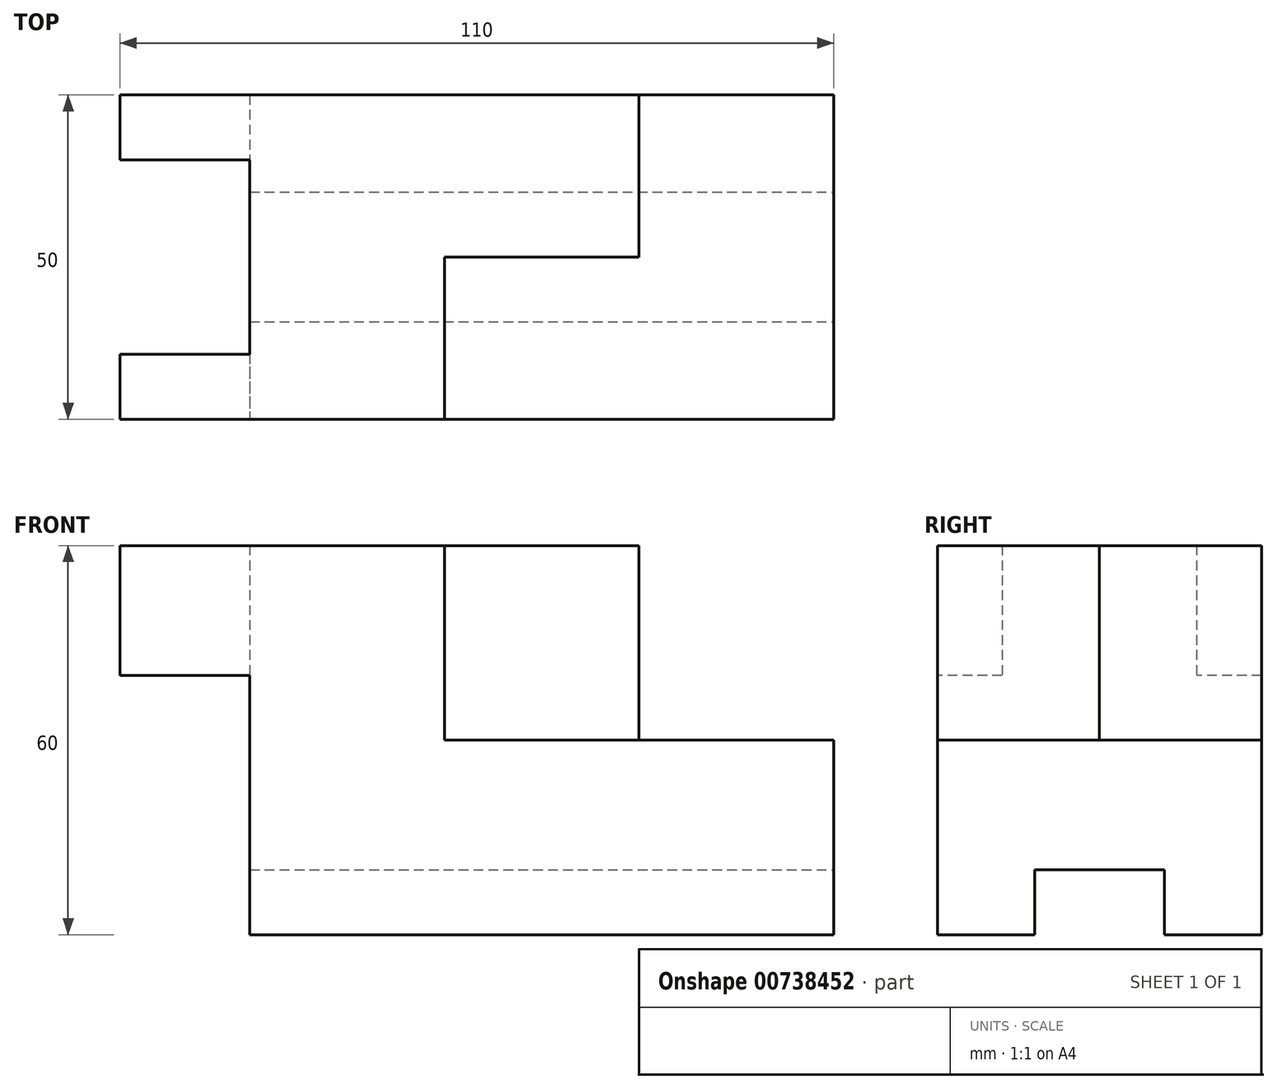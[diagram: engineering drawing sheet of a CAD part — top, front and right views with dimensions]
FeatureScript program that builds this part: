
annotation { "Feature Type Name" : "Feature", "Feature Type Description" : "" }
export const myFeature = defineFeature(function(context is Context, id is Id, definition is map)
    precondition{}
    {
        {
            var Q0;
            Q0=qCreatedBy(makeId("Front.planeOp"),FACE);
            var sketch = newSketch(context, id + "F0", { "sketchPlane" : qUnion([Q0])});
            skLineSegment(sketch, "E0", {"start": v(0, 0) * mm, "end": v(-90, 0) * mm});
            skLineSegment(sketch, "E1", {"start": v(-90, 0) * mm, "end": v(-90, 40) * mm});
            skLineSegment(sketch, "E2", {"start": v(-90, 40) * mm, "end": v(-110, 40) * mm});
            skLineSegment(sketch, "E3", {"start": v(-110, 40) * mm, "end": v(-110, 60) * mm});
            skLineSegment(sketch, "E4", {"start": v(-110, 60) * mm, "end": v(-30, 60) * mm});
            skLineSegment(sketch, "E5", {"start": v(-30, 60) * mm, "end": v(-30, 30) * mm});
            skLineSegment(sketch, "E6", {"start": v(-30, 30) * mm, "end": v(0, 30) * mm});
            skLineSegment(sketch, "E7", {"start": v(0, 30) * mm, "end": v(0, 0) * mm});
            skSolve(sketch);
        }
        {
            var Q0;
            Q0 = qSketchRegion(id + "F0", true);
            extrude(context, id + "F1", {"entities" : qUnion([Q0]), "oppositeDirection" : true, "depth" : 50 * mm, "offsetDistance" : 25 * mm});
        }
        {
            var Q0;
            Q0=makeQuery(id+"F1.opExtrude","SWEPT_FACE",FACE,{"disambiguationData":[OSD([sQuery(id+"F0.wireOp",EDGE,"E3")])]});
            var sketch = newSketch(context, id + "F2", { "sketchPlane" : qUnion([Q0])});
            skLineSegment(sketch, "E8.bottom", {"start": v(-40, 80) * mm, "end": v(-10, 80) * mm});
            skLineSegment(sketch, "E8.top", {"start": v(-40, 40) * mm, "end": v(-10, 40) * mm});
            skLineSegment(sketch, "E8.left", {"start": v(-40, 80) * mm, "end": v(-40, 40) * mm});
            skLineSegment(sketch, "E8.right", {"start": v(-10, 80) * mm, "end": v(-10, 40) * mm});
            skPoint(sketch, "E8.middle", {"position": v(-25, 60) * mm});
            skSolve(sketch);
        }
        {
            var Q0;
            Q0 = qSketchRegion(id + "F2", true);
            extrude(context, id + "F3", {"entities" : qUnion([Q0]), "operationType" : NewBodyOperationType.REMOVE, "oppositeDirection" : true, "depth" : 20 * mm, "offsetDistance" : 25 * mm});
        }
        {
            var Q0;
            Q0=makeQuery(id+"F1.opExtrude","SWEPT_FACE",FACE,{"disambiguationData":[OSD([sQuery(id+"F0.wireOp",EDGE,"E4")])]});
            var sketch = newSketch(context, id + "F4", { "sketchPlane" : qUnion([Q0])});
            skLineSegment(sketch, "E9.bottom", {"start": v(-30, 0) * mm, "end": v(-60, 0) * mm});
            skLineSegment(sketch, "E9.top", {"start": v(-30, 25) * mm, "end": v(-60, 25) * mm});
            skLineSegment(sketch, "E9.left", {"start": v(-30, 0) * mm, "end": v(-30, 25) * mm});
            skLineSegment(sketch, "E9.right", {"start": v(-60, 0) * mm, "end": v(-60, 25) * mm});
            skSolve(sketch);
        }
        {
            var Q0;
            Q0 = qSketchRegion(id + "F4", true);
            extrude(context, id + "F5", {"entities" : qUnion([Q0]), "operationType" : NewBodyOperationType.REMOVE, "oppositeDirection" : true, "depth" : 30 * mm, "offsetDistance" : 25 * mm, "hasSecondDirection" : true, "secondDirectionOppositeDirection" : false, "secondDirectionDepth" : 25 * mm});
        }
        {
            var Q0;
            Q0=makeQuery(id+"F1.opExtrude","SWEPT_FACE",FACE,{"disambiguationData":[OSD([sQuery(id+"F0.wireOp",EDGE,"E7")])]});
            var sketch = newSketch(context, id + "F6", { "sketchPlane" : qUnion([Q0])});
            skLineSegment(sketch, "E10.bottom", {"start": v(15, 10) * mm, "end": v(35, 10) * mm});
            skLineSegment(sketch, "E10.top", {"start": v(15, -10) * mm, "end": v(35, -10) * mm});
            skLineSegment(sketch, "E10.left", {"start": v(15, 10) * mm, "end": v(15, -10) * mm});
            skLineSegment(sketch, "E10.right", {"start": v(35, 10) * mm, "end": v(35, -10) * mm});
            skPoint(sketch, "E10.middle", {"position": v(25, 0) * mm});
            skSolve(sketch);
        }
        {
            var Q0;
            Q0 = qSketchRegion(id + "F6", true);
            extrude(context, id + "F7", {"entities" : qUnion([Q0]), "operationType" : NewBodyOperationType.REMOVE, "oppositeDirection" : true, "depth" : 90 * mm, "offsetDistance" : 25 * mm});
        }
    });
